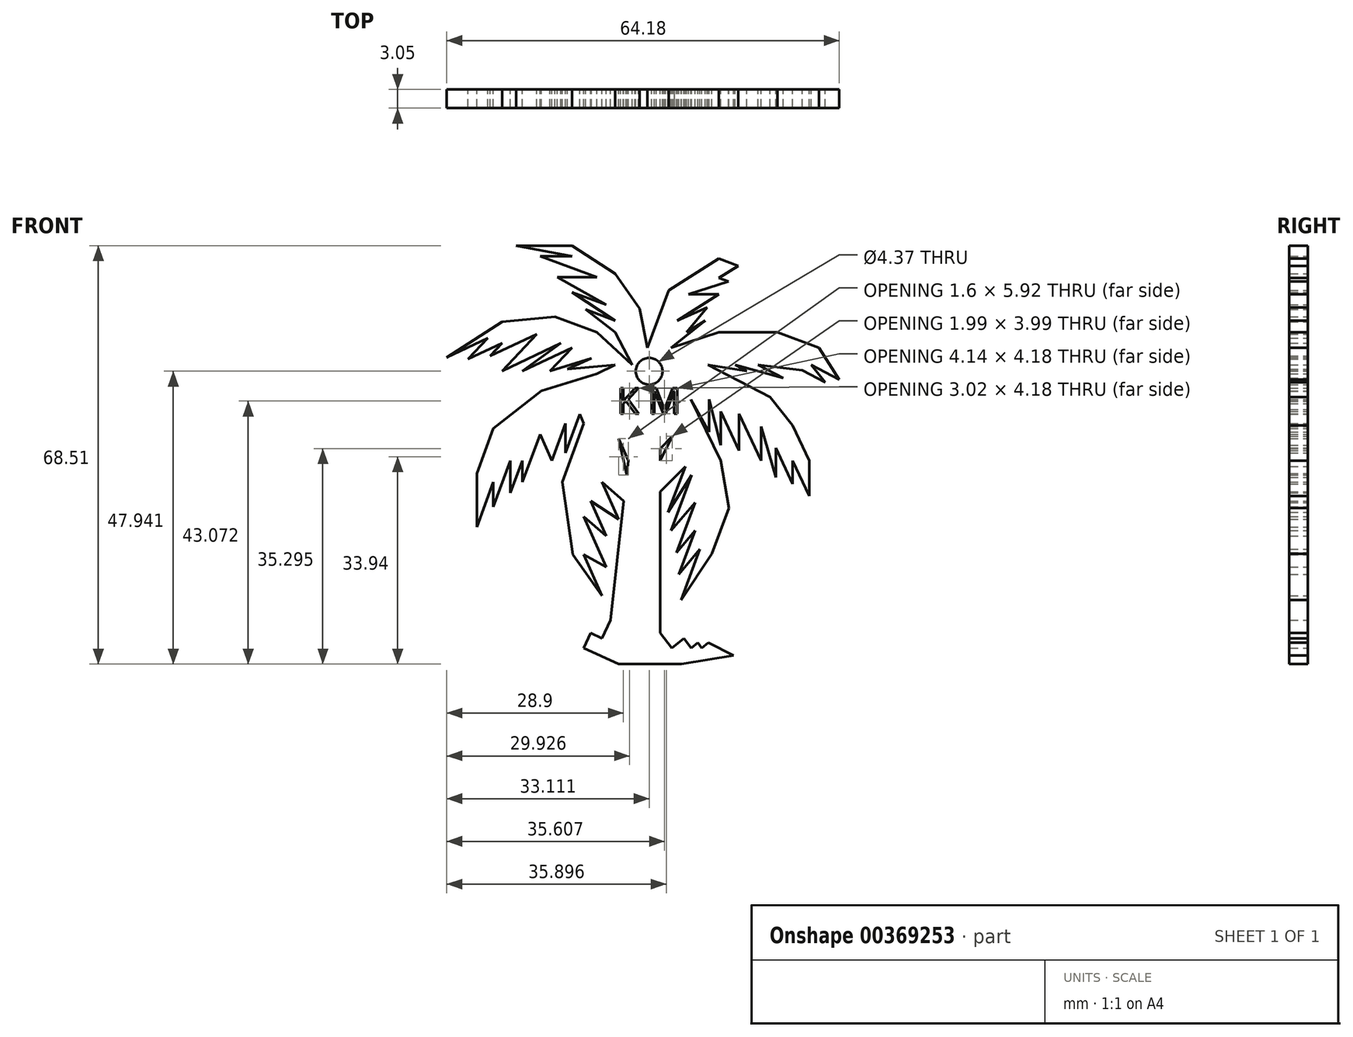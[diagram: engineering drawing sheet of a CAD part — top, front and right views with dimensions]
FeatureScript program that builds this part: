
annotation { "Feature Type Name" : "Feature", "Feature Type Description" : "" }
export const myFeature = defineFeature(function(context is Context, id is Id, definition is map)
    precondition{}
    {
        {
            var Q0;
            Q0=qCreatedBy(makeId("Front.planeOp"),FACE);
            var sketch = newSketch(context, id + "F0", { "sketchPlane" : qUnion([Q0])});
            skLineSegment(sketch, "E0", {"start": v(12, -31.88) * mm, "end": v(3.5, -33.3) * mm});
            skLineSegment(sketch, "E1", {"start": v(3.5, -33.3) * mm, "end": v(-6.8, -33.3) * mm});
            skLineSegment(sketch, "E2", {"start": v(-6.8, -33.3) * mm, "end": v(-12.47, -30.64) * mm});
            skLineSegment(sketch, "E3", {"start": v(-12.47, -30.64) * mm, "end": v(-11.34, -28.2) * mm});
            skLineSegment(sketch, "E4", {"start": v(-11.34, -28.2) * mm, "end": v(-9.5, -29.07) * mm});
            skLineSegment(sketch, "E5", {"start": v(-9.5, -29.07) * mm, "end": v(-8.1, -26.1) * mm});
            skLineSegment(sketch, "E6", {"start": v(-8.1, -26.1) * mm, "end": v(-8.1, -29.07) * mm});
            skLineSegment(sketch, "E7", {"start": v(-8.1, -29.07) * mm, "end": v(-6.8, -28.2) * mm});
            skLineSegment(sketch, "E8", {"start": v(-6.8, -28.2) * mm, "end": v(-3.96, -29.07) * mm});
            skLineSegment(sketch, "E9", {"start": v(-3.96, -29.07) * mm, "end": v(0, -28.2) * mm});
            skLineSegment(sketch, "E10", {"start": v(0, -28.2) * mm, "end": v(1.9, -30.64) * mm});
            skLineSegment(sketch, "E11", {"start": v(1.9, -30.64) * mm, "end": v(3.9, -29.07) * mm});
            skLineSegment(sketch, "E12", {"start": v(3.9, -29.07) * mm, "end": v(5.12, -30.64) * mm});
            skLineSegment(sketch, "E13", {"start": v(5.12, -30.64) * mm, "end": v(6.18, -29.81) * mm});
            skLineSegment(sketch, "E14", {"start": v(6.18, -29.81) * mm, "end": v(6.82, -30.64) * mm});
            skLineSegment(sketch, "E15", {"start": v(6.82, -30.64) * mm, "end": v(7.88, -29.81) * mm});
            skLineSegment(sketch, "E16", {"start": v(7.88, -29.81) * mm, "end": v(12, -31.88) * mm});
            skLineSegment(sketch, "E17", {"start": v(-8.1, -26.1) * mm, "end": v(-5.2, 0) * mm});
            skLineSegment(sketch, "E18", {"start": v(-5.2, 0) * mm, "end": v(-6.8, 3.6) * mm});
            skLineSegment(sketch, "E19", {"start": v(-6.8, 3.6) * mm, "end": v(-5.46, -2.32) * mm});
            skLineSegment(sketch, "E20", {"start": v(-5.46, -2.32) * mm, "end": v(-8.1, 0) * mm});
            skLineSegment(sketch, "E21", {"start": v(-8.1, 0) * mm, "end": v(-5.94, -6.62) * mm});
            skLineSegment(sketch, "E22", {"start": v(-5.94, -6.62) * mm, "end": v(-9.5, -3.5) * mm});
            skLineSegment(sketch, "E23", {"start": v(-9.5, -3.5) * mm, "end": v(-6.8, -9.58) * mm});
            skLineSegment(sketch, "E24", {"start": v(-6.8, -9.58) * mm, "end": v(-11.34, -6.62) * mm});
            skLineSegment(sketch, "E25", {"start": v(-11.34, -6.62) * mm, "end": v(-8.82, -12.31) * mm});
            skLineSegment(sketch, "E26", {"start": v(-8.82, -12.31) * mm, "end": v(-12.47, -9.17) * mm});
            skLineSegment(sketch, "E27", {"start": v(-12.47, -9.17) * mm, "end": v(-8.82, -17.43) * mm});
            skLineSegment(sketch, "E28", {"start": v(-8.82, -17.43) * mm, "end": v(-12.47, -15.38) * mm});
            skLineSegment(sketch, "E29", {"start": v(-12.47, -15.38) * mm, "end": v(-9.5, -22.1) * mm});
            skLineSegment(sketch, "E30", {"start": v(-9.5, -22.1) * mm, "end": v(-14.25, -15.38) * mm});
            skLineSegment(sketch, "E31", {"start": v(-14.25, -15.38) * mm, "end": v(-16.02, -3.5) * mm});
            skLineSegment(sketch, "E32", {"start": v(-16.02, -3.5) * mm, "end": v(-12.47, 6.09) * mm});
            skLineSegment(sketch, "E33", {"start": v(-12.47, 6.09) * mm, "end": v(-9.5, 9.1) * mm});
            skLineSegment(sketch, "E34", {"start": v(-9.5, 9.1) * mm, "end": v(-12.47, 6.09) * mm});
            skLineSegment(sketch, "E35", {"start": v(-12.47, 6.09) * mm, "end": v(-13.14, 7.6) * mm});
            skPoint(sketch, "E35.endSnap0", {"position": v(-10.99, 7.6) * mm});
            skLineSegment(sketch, "E36", {"start": v(-13.14, 7.6) * mm, "end": v(-15.48, 1.3) * mm});
            skPoint(sketch, "E36.endSnap0", {"position": v(-14.25, 1.3) * mm});
            skLineSegment(sketch, "E37", {"start": v(-15.48, 1.3) * mm, "end": v(-15.48, 6.09) * mm});
            skLineSegment(sketch, "E38", {"start": v(-15.48, 6.09) * mm, "end": v(-17.73, 0) * mm});
            skLineSegment(sketch, "E39", {"start": v(-17.73, 0) * mm, "end": v(-19.64, 4.3) * mm});
            skLineSegment(sketch, "E40", {"start": v(-19.64, 4.3) * mm, "end": v(-22.52, -3.5) * mm});
            skLineSegment(sketch, "E41", {"start": v(-22.52, -3.5) * mm, "end": v(-22.52, 0) * mm});
            skLineSegment(sketch, "E42", {"start": v(-22.52, 0) * mm, "end": v(-24.48, -5.29) * mm});
            skLineSegment(sketch, "E43", {"start": v(-24.48, -5.29) * mm, "end": v(-24.48, 0) * mm});
            skLineSegment(sketch, "E44", {"start": v(-24.48, 0) * mm, "end": v(-27.27, -7.53) * mm});
            skLineSegment(sketch, "E45", {"start": v(-27.27, -7.53) * mm, "end": v(-27.27, -3.5) * mm});
            skLineSegment(sketch, "E46", {"start": v(-27.27, -3.5) * mm, "end": v(-29.99, -10.83) * mm});
            skLineSegment(sketch, "E47", {"start": v(-29.99, -10.83) * mm, "end": v(-29.99, -2.07) * mm});
            skLineSegment(sketch, "E48", {"start": v(-29.99, -2.07) * mm, "end": v(-27.27, 5.26) * mm});
            skLineSegment(sketch, "E49", {"start": v(-27.27, 5.26) * mm, "end": v(-19.4, 11.4) * mm});
            skLineSegment(sketch, "E50", {"start": v(-19.4, 11.4) * mm, "end": v(-10.35, 14.25) * mm});
            skLineSegment(sketch, "E51", {"start": v(-10.35, 14.25) * mm, "end": v(-7.33, 15.67) * mm});
            skLineSegment(sketch, "E52", {"start": v(-7.33, 15.67) * mm, "end": v(-15.14, 14.96) * mm});
            skPoint(sketch, "E52.endSnap0", {"position": v(-8.84, 14.96) * mm});
            skLineSegment(sketch, "E53", {"start": v(-15.14, 14.96) * mm, "end": v(-11.23, 16.8) * mm});
            skPoint(sketch, "E53.endSnap0", {"position": v(-11.23, 15.31) * mm});
            skLineSegment(sketch, "E54", {"start": v(-11.23, 16.8) * mm, "end": v(-18.02, 14.67) * mm});
            skLineSegment(sketch, "E55", {"start": v(-18.02, 14.67) * mm, "end": v(-14.43, 18.5) * mm});
            skLineSegment(sketch, "E56", {"start": v(-14.43, 18.5) * mm, "end": v(-22.52, 14.7) * mm});
            skLineSegment(sketch, "E57", {"start": v(-22.52, 14.7) * mm, "end": v(-16.22, 19.21) * mm});
            skPoint(sketch, "E57.endSnap0", {"position": v(-16.22, 16.59) * mm});
            skLineSegment(sketch, "E58", {"start": v(-16.22, 19.21) * mm, "end": v(-25.83, 14.7) * mm});
            skLineSegment(sketch, "E59", {"start": v(-25.83, 14.7) * mm, "end": v(-20.2, 20.71) * mm});
            skLineSegment(sketch, "E60", {"start": v(-20.2, 20.71) * mm, "end": v(-27.82, 17.13) * mm});
            skLineSegment(sketch, "E61", {"start": v(-27.82, 17.13) * mm, "end": v(-25.83, 19.26) * mm});
            skLineSegment(sketch, "E62", {"start": v(-25.83, 19.26) * mm, "end": v(-31.42, 16.63) * mm});
            skLineSegment(sketch, "E63", {"start": v(-31.42, 16.63) * mm, "end": v(-28.21, 20.06) * mm});
            skLineSegment(sketch, "E64", {"start": v(-28.21, 20.06) * mm, "end": v(-34.9, 16.91) * mm});
            skLineSegment(sketch, "E65", {"start": v(-34.9, 16.91) * mm, "end": v(-25.83, 22.76) * mm});
            skLineSegment(sketch, "E66", {"start": v(-25.83, 22.76) * mm, "end": v(-17.18, 23.55) * mm});
            skLineSegment(sketch, "E67", {"start": v(-17.18, 23.55) * mm, "end": v(-10.35, 21.02) * mm});
            skLineSegment(sketch, "E68", {"start": v(-10.35, 21.02) * mm, "end": v(-4.57, 15.67) * mm});
            skLineSegment(sketch, "E69", {"start": v(-4.57, 15.67) * mm, "end": v(-7.33, 21.02) * mm});
            skLineSegment(sketch, "E70", {"start": v(-7.33, 21.02) * mm, "end": v(-12.2, 24.75) * mm});
            skLineSegment(sketch, "E71", {"start": v(-12.2, 24.75) * mm, "end": v(-7.33, 22.94) * mm});
            skLineSegment(sketch, "E72", {"start": v(-7.33, 22.94) * mm, "end": v(-14.43, 27.58) * mm});
            skLineSegment(sketch, "E73", {"start": v(-14.43, 27.58) * mm, "end": v(-8.84, 25.51) * mm});
            skLineSegment(sketch, "E74", {"start": v(-8.84, 25.51) * mm, "end": v(-16.81, 30.07) * mm});
            skLineSegment(sketch, "E75", {"start": v(-16.81, 30.07) * mm, "end": v(-10.35, 30.07) * mm});
            skLineSegment(sketch, "E76", {"start": v(-10.35, 30.07) * mm, "end": v(-19.6, 33.5) * mm});
            skLineSegment(sketch, "E77", {"start": v(-19.6, 33.5) * mm, "end": v(-14.43, 33.5) * mm});
            skLineSegment(sketch, "E78", {"start": v(-14.43, 33.5) * mm, "end": v(-23.55, 35.21) * mm});
            skLineSegment(sketch, "E79", {"start": v(-23.55, 35.21) * mm, "end": v(-14.43, 35.21) * mm});
            skLineSegment(sketch, "E80", {"start": v(-14.43, 35.21) * mm, "end": v(-7.33, 30.6) * mm});
            skLineSegment(sketch, "E81", {"start": v(-7.33, 30.6) * mm, "end": v(-3.33, 24.92) * mm});
            skLineSegment(sketch, "E82", {"start": v(-3.33, 24.92) * mm, "end": v(-2.09, 18.5) * mm});
            skLineSegment(sketch, "E83", {"start": v(-2.09, 18.5) * mm, "end": v(1.4, 27.9) * mm});
            skLineSegment(sketch, "E84", {"start": v(1.4, 27.9) * mm, "end": v(9.62, 33.08) * mm});
            skLineSegment(sketch, "E85", {"start": v(9.62, 33.08) * mm, "end": v(12.8, 31.9) * mm});
            skLineSegment(sketch, "E86", {"start": v(12.8, 31.9) * mm, "end": v(9.62, 29.9) * mm});
            skLineSegment(sketch, "E87", {"start": v(9.62, 29.9) * mm, "end": v(11.21, 29.32) * mm});
            skPoint(sketch, "E87.endSnap0", {"position": v(11.21, 30.9) * mm});
            skLineSegment(sketch, "E88", {"start": v(11.21, 29.32) * mm, "end": v(4.65, 27.23) * mm});
            skLineSegment(sketch, "E89", {"start": v(4.65, 27.23) * mm, "end": v(9.62, 27.23) * mm});
            skLineSegment(sketch, "E90", {"start": v(9.62, 27.23) * mm, "end": v(2.82, 22.94) * mm});
            skLineSegment(sketch, "E91", {"start": v(2.82, 22.94) * mm, "end": v(7.67, 25.09) * mm});
            skPoint(sketch, "E91.endSnap0", {"position": v(6.22, 25.09) * mm});
            skLineSegment(sketch, "E92", {"start": v(7.67, 25.09) * mm, "end": v(4.3, 21.02) * mm});
            skLineSegment(sketch, "E93", {"start": v(4.3, 21.02) * mm, "end": v(7.35, 22.94) * mm});
            skLineSegment(sketch, "E94", {"start": v(7.35, 22.94) * mm, "end": v(1.82, 18.5) * mm});
            skLineSegment(sketch, "E95", {"start": v(1.82, 18.5) * mm, "end": v(9.62, 21.02) * mm});
            skLineSegment(sketch, "E96", {"start": v(9.62, 21.02) * mm, "end": v(14.94, 21.02) * mm});
            skLineSegment(sketch, "E97", {"start": v(14.94, 21.02) * mm, "end": v(19.2, 21.02) * mm});
            skLineSegment(sketch, "E98", {"start": v(19.2, 21.02) * mm, "end": v(26, 18.5) * mm});
            skLineSegment(sketch, "E99", {"start": v(26, 18.5) * mm, "end": v(29.28, 13.28) * mm});
            skLineSegment(sketch, "E100", {"start": v(29.28, 13.28) * mm, "end": v(24.7, 15.67) * mm});
            skLineSegment(sketch, "E101", {"start": v(24.7, 15.67) * mm, "end": v(27, 12.86) * mm});
            skPoint(sketch, "E101.endSnap0", {"position": v(27, 14.47) * mm});
            skLineSegment(sketch, "E102", {"start": v(27, 12.86) * mm, "end": v(19.54, 16.74) * mm});
            skLineSegment(sketch, "E103", {"start": v(19.54, 16.74) * mm, "end": v(23.27, 14.8) * mm});
            skLineSegment(sketch, "E104", {"start": v(23.27, 14.8) * mm, "end": v(16, 15.67) * mm});
            skLineSegment(sketch, "E105", {"start": v(16, 15.67) * mm, "end": v(20.16, 13.5) * mm});
            skLineSegment(sketch, "E106", {"start": v(20.16, 13.5) * mm, "end": v(12.28, 15.67) * mm});
            skLineSegment(sketch, "E107", {"start": v(12.28, 15.67) * mm, "end": v(16.08, 13.69) * mm});
            skLineSegment(sketch, "E108", {"start": v(16.08, 13.69) * mm, "end": v(9.96, 16.88) * mm});
            skLineSegment(sketch, "E109", {"start": v(9.96, 16.88) * mm, "end": v(14.18, 14.68) * mm});
            skLineSegment(sketch, "E110", {"start": v(14.18, 14.68) * mm, "end": v(7.85, 15.67) * mm});
            skLineSegment(sketch, "E111", {"start": v(7.85, 15.67) * mm, "end": v(13.4, 12.78) * mm});
            skLineSegment(sketch, "E112", {"start": v(13.4, 12.78) * mm, "end": v(17.99, 10.39) * mm});
            skLineSegment(sketch, "E113", {"start": v(17.99, 10.39) * mm, "end": v(21.68, 5.76) * mm});
            skLineSegment(sketch, "E114", {"start": v(21.68, 5.76) * mm, "end": v(24.4, 0) * mm});
            skLineSegment(sketch, "E115", {"start": v(24.4, 0) * mm, "end": v(24.4, -5.77) * mm});
            skLineSegment(sketch, "E116", {"start": v(24.4, -5.77) * mm, "end": v(21.68, 0) * mm});
            skLineSegment(sketch, "E117", {"start": v(21.68, 0) * mm, "end": v(21.68, -3.82) * mm});
            skLineSegment(sketch, "E118", {"start": v(21.68, -3.82) * mm, "end": v(18.9, 2.08) * mm});
            skLineSegment(sketch, "E119", {"start": v(18.9, 2.08) * mm, "end": v(18.9, -2.75) * mm});
            skLineSegment(sketch, "E120", {"start": v(18.9, -2.75) * mm, "end": v(16.54, 5.59) * mm});
            skLineSegment(sketch, "E121", {"start": v(16.54, 5.59) * mm, "end": v(16.54, 0) * mm});
            skLineSegment(sketch, "E122", {"start": v(16.54, 0) * mm, "end": v(12.92, 7.68) * mm});
            skLineSegment(sketch, "E123", {"start": v(12.92, 7.68) * mm, "end": v(12.92, 1.68) * mm});
            skLineSegment(sketch, "E124", {"start": v(12.92, 1.68) * mm, "end": v(9.92, 8.07) * mm});
            skLineSegment(sketch, "E125", {"start": v(9.92, 8.07) * mm, "end": v(9.92, 2.57) * mm});
            skLineSegment(sketch, "E126", {"start": v(9.92, 2.57) * mm, "end": v(8.02, 10.02) * mm});
            skLineSegment(sketch, "E127", {"start": v(8.02, 10.02) * mm, "end": v(8.02, 4.7) * mm});
            skLineSegment(sketch, "E128", {"start": v(8.02, 4.7) * mm, "end": v(5, 10.02) * mm});
            skLineSegment(sketch, "E129", {"start": v(5, 10.02) * mm, "end": v(9.92, 0) * mm});
            skLineSegment(sketch, "E130", {"start": v(9.92, 0) * mm, "end": v(11.22, -7.72) * mm});
            skLineSegment(sketch, "E131", {"start": v(11.22, -7.72) * mm, "end": v(8.44, -15.22) * mm});
            skLineSegment(sketch, "E132", {"start": v(8.44, -15.22) * mm, "end": v(3.41, -22.8) * mm});
            skLineSegment(sketch, "E133", {"start": v(3.41, -22.8) * mm, "end": v(6.5, -14.47) * mm});
            skLineSegment(sketch, "E134", {"start": v(6.5, -14.47) * mm, "end": v(3.06, -18.63) * mm});
            skPoint(sketch, "E134.endSnap0", {"position": v(4.96, -18.63) * mm});
            skLineSegment(sketch, "E135", {"start": v(3.06, -18.63) * mm, "end": v(5.73, -11.41) * mm});
            skLineSegment(sketch, "E136", {"start": v(5.73, -11.41) * mm, "end": v(2.7, -15.02) * mm});
            skPoint(sketch, "E136.endSnap0", {"position": v(4.4, -15.02) * mm});
            skLineSegment(sketch, "E137", {"start": v(2.7, -15.02) * mm, "end": v(5.73, -6.84) * mm});
            skLineSegment(sketch, "E138", {"start": v(5.73, -6.84) * mm, "end": v(1.82, -11.41) * mm});
            skLineSegment(sketch, "E139", {"start": v(1.82, -11.41) * mm, "end": v(5.18, -2.32) * mm});
            skLineSegment(sketch, "E140", {"start": v(5.18, -2.32) * mm, "end": v(1.28, -8.43) * mm});
            skLineSegment(sketch, "E141", {"start": v(1.28, -8.43) * mm, "end": v(4.12, -0.98) * mm});
            skLineSegment(sketch, "E142", {"start": v(4.12, -0.98) * mm, "end": v(0, -5.06) * mm});
            skLineSegment(sketch, "E143", {"start": v(0, -5.06) * mm, "end": v(4.12, 2.92) * mm});
            skLineSegment(sketch, "E144", {"start": v(4.12, 2.92) * mm, "end": v(0, 0) * mm});
            skLineSegment(sketch, "E145", {"start": v(0, 0) * mm, "end": v(2, 3.99) * mm});
            skLineSegment(sketch, "E146", {"start": v(2, 3.99) * mm, "end": v(0, 2) * mm});
            skPoint(sketch, "E146.endSnap0", {"position": v(1, 2) * mm});
            skLineSegment(sketch, "E147", {"start": v(0, 2) * mm, "end": v(0, -28.2) * mm});
            skCircle(sketch, "E148", {"center": v(-1.79, 14.64) * mm, "radius": 2.19 * mm});
            skText(sketch, "E149", { "text": "K M", "fontName": "OpenSans-Regular.ttf"});
            const initialGuessF0  = {"E149": [-0.00706, 0.00768, 1, 0, 0.00422]};
            skSetInitialGuess(sketch, initialGuessF0);
            skSolve(sketch);
        }
        {
            var Q0;
            Q0 = qSketchRegion(id + "F0", true);
            extrude(context, id + "F1", {"entities" : qUnion([Q0]), "depth" : 3.05 * mm});
        }
    });
